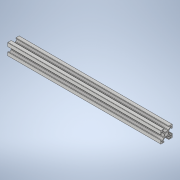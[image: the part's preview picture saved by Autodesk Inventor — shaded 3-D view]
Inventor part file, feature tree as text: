
AUTODESK INVENTOR PART (.ipt)
format: ipt  version: 2020 (Build 240168000, 168)  size: 263,680 bytes
history: mixed  units: mm
features: sketch x3, other x2, extrude x1, imported_body x1
ambient origin geometry x8: Origin, YZ Plane, XZ Plane, XY Plane, X Axis, Y Axis, Z Axis, Center Point
bodies: Body1 (imported_parasolid)
feature tree (7):
  other  "Sólido1"
  extrude  "Extrusión1"  Depth=261.0mm
  sketch  "Boceto3"
  sketch  "Boceto7"
  sketch  "Boceto1"  dims[d0=161.0mm d1=0.0mm d8=261.0mm]
  other  "Quadrado PF20-01 - PERFIL 2020 BÁSICO(1)"
  imported_body  NMx_Import_Brep_tag  [imported B-rep: ~59 faces, bbox_mm=[261.0, 20.0, 20.0]]
